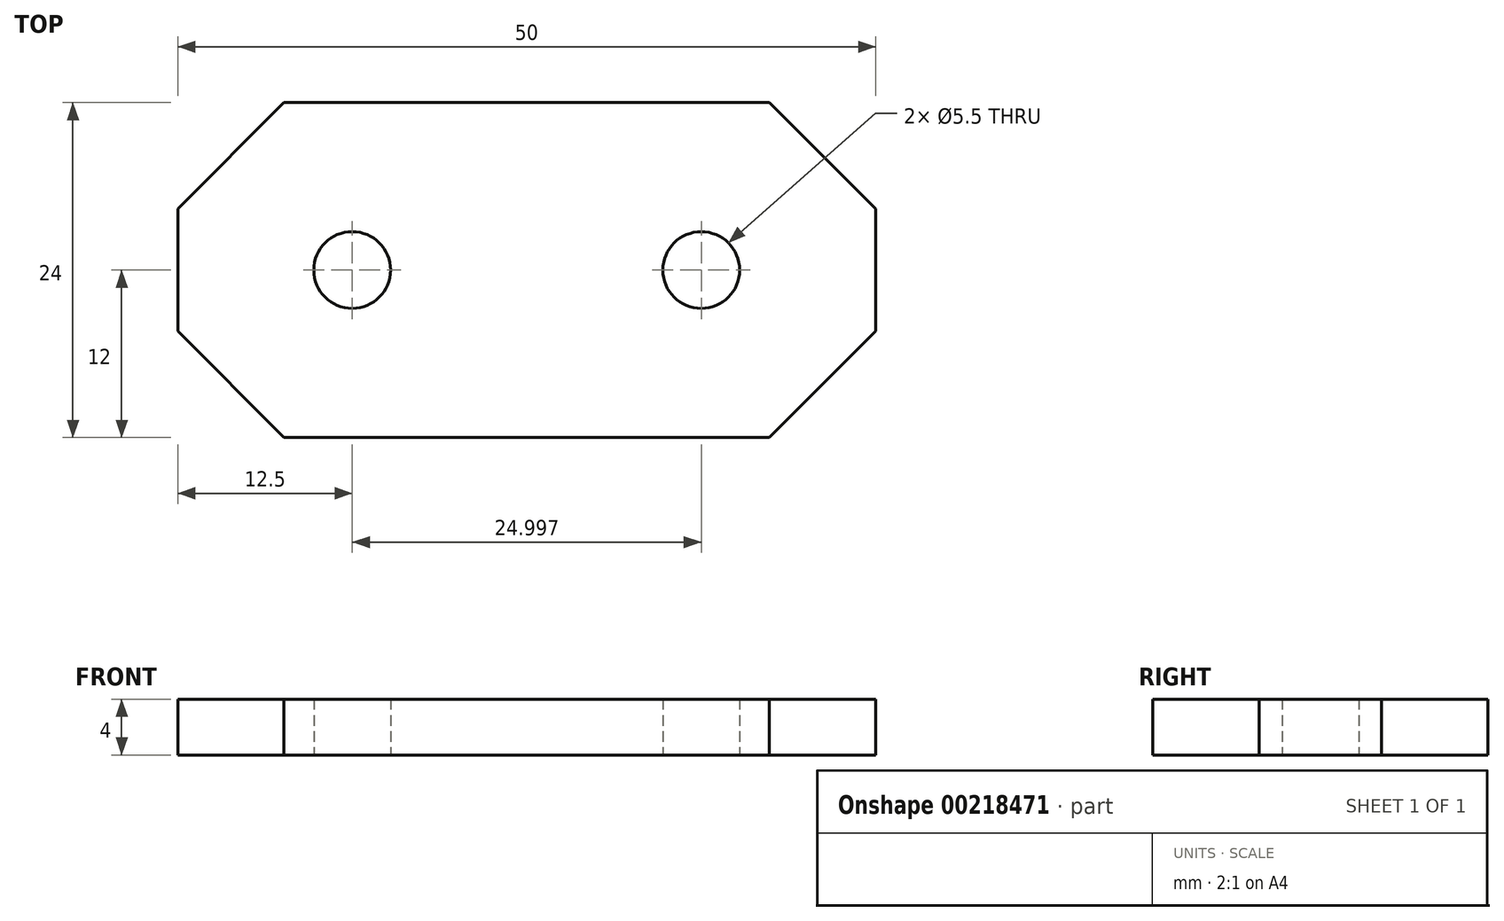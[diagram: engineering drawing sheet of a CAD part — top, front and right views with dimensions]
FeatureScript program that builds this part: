
annotation { "Feature Type Name" : "Feature", "Feature Type Description" : "" }
export const myFeature = defineFeature(function(context is Context, id is Id, definition is map)
    precondition{}
    {
        {
            var Q0;
            Q0=qCreatedBy(makeId("Top.planeOp"),FACE);
            var sketch = newSketch(context, id + "F0", { "sketchPlane" : qUnion([Q0])});
            skLineSegment(sketch, "E0.bottom", {"start": v(25, 12) * mm, "end": v(-25, 12) * mm});
            skLineSegment(sketch, "E0.top", {"start": v(25, -12) * mm, "end": v(-25, -12) * mm});
            skLineSegment(sketch, "E0.left", {"start": v(25, 12) * mm, "end": v(25, -12) * mm});
            skLineSegment(sketch, "E0.right", {"start": v(-25, 12) * mm, "end": v(-25, -12) * mm});
            skPoint(sketch, "E0.middle", {"position": v(0, 0) * mm});
            skLineSegment(sketch, "E1", {"start": v(0, 0) * mm, "end": v(-12.5, 0) * mm});
            skLineSegment(sketch, "E2", {"start": v(0, 0) * mm, "end": v(12.5, 0) * mm});
            skCircle(sketch, "E3", {"center": v(-12.5, 0) * mm, "radius": 2.75 * mm});
            skCircle(sketch, "E4", {"center": v(12.5, 0) * mm, "radius": 2.75 * mm});
            skSolve(sketch);
        }
        {
            var Q0;
            Q0=makeQuery(id+"F0.imprint","IMPRINT",FACE,{"disambiguationData":[TD([[makeQuery(id+"F0.imprint","IMPRINT",EDGE,{"derivedFrom":sQuery(id+"F0.wireOp",EDGE,"E0.bottom")}),1.0]])]});
            extrude(context, id + "F1", {"entities" : qUnion([Q0]), "depth" : 4 * mm});
        }
        {
            var Q0;
            Q0=makeQuery(id+"F1.opExtrude","SWEPT_EDGE",EDGE,{"disambiguationData":[OSD([sQuery(id+"F0.wireOp",EDGE,"E0.bottom"),sQuery(id+"F0.wireOp",EDGE,"E0.right")])]});
            var Q1;
            Q1=makeQuery(id+"F1.opExtrude","SWEPT_EDGE",EDGE,{"disambiguationData":[OSD([sQuery(id+"F0.wireOp",EDGE,"E0.top"),sQuery(id+"F0.wireOp",EDGE,"E0.right")])]});
            var Q2;
            Q2=makeQuery(id+"F1.opExtrude","SWEPT_EDGE",EDGE,{"disambiguationData":[OSD([sQuery(id+"F0.wireOp",EDGE,"E0.top"),sQuery(id+"F0.wireOp",EDGE,"E0.left")])]});
            var Q3;
            Q3=makeQuery(id+"F1.opExtrude","SWEPT_EDGE",EDGE,{"disambiguationData":[OSD([sQuery(id+"F0.wireOp",EDGE,"E0.bottom"),sQuery(id+"F0.wireOp",EDGE,"E0.left")])]});
            chamfer(context, id + "F2", {"entities" : qUnion([Q0, Q1, Q2, Q3]), "width" : 7.62 * mm, "tangentPropagation" : true});
        }
    });
